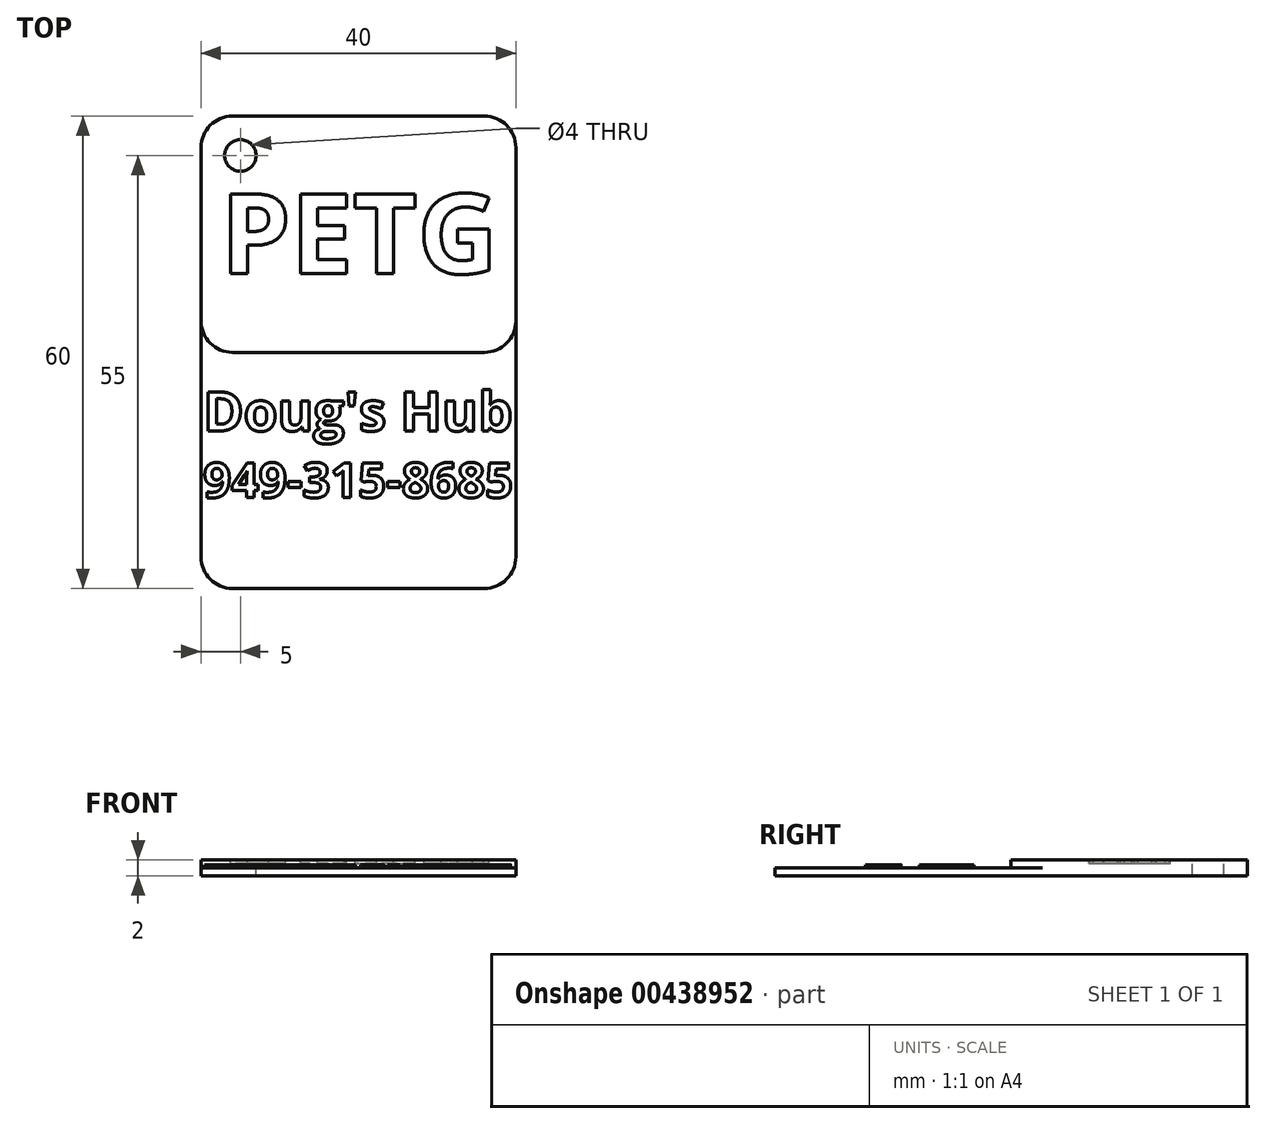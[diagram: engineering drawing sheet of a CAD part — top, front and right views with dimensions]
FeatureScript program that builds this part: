
annotation { "Feature Type Name" : "Feature", "Feature Type Description" : "" }
export const myFeature = defineFeature(function(context is Context, id is Id, definition is map)
    precondition{}
    {
        {
            var Q0;
            Q0=qCreatedBy(makeId("Top.planeOp"),FACE);
            var sketch = newSketch(context, id + "F0", { "sketchPlane" : qUnion([Q0])});
            skLineSegment(sketch, "E0.bottom", {"start": v(0, 0) * mm, "end": v(40, 0) * mm});
            skLineSegment(sketch, "E0.top", {"start": v(0, 60) * mm, "end": v(40, 60) * mm});
            skLineSegment(sketch, "E0.left", {"start": v(0, 0) * mm, "end": v(0, 60) * mm});
            skLineSegment(sketch, "E0.right", {"start": v(40, 0) * mm, "end": v(40, 60) * mm});
            skSolve(sketch);
        }
        {
            var Q0;
            Q0=qSketchRegion(id+"F0",true);
            extrude(context, id + "F1", {"entities" : qUnion([Q0]), "depth" : 1 * mm});
        }
        {
            var Q0;
            Q0=makeQuery(id+"F1.opExtrude","CAP_FACE",FACE,{"disambiguationData":[OSD([sQuery(id+"F0.wireOp",EDGE,"E0.bottom"),sQuery(id+"F0.wireOp",EDGE,"E0.top"),sQuery(id+"F0.wireOp",EDGE,"E0.left"),sQuery(id+"F0.wireOp",EDGE,"E0.right")])],"isStart":false});
            var sketch = newSketch(context, id + "F2", { "sketchPlane" : qUnion([Q0])});
            skLineSegment(sketch, "E1.bottom", {"start": v(0, 60) * mm, "end": v(40, 60) * mm});
            skLineSegment(sketch, "E1.top", {"start": v(0, 30) * mm, "end": v(40, 30) * mm});
            skLineSegment(sketch, "E1.left", {"start": v(0, 60) * mm, "end": v(0, 30) * mm});
            skLineSegment(sketch, "E1.right", {"start": v(40, 60) * mm, "end": v(40, 30) * mm});
            skSolve(sketch);
        }
        {
            var Q0;
            Q0=qSketchRegion(id+"F2",true);
            extrude(context, id + "F3", {"entities" : qUnion([Q0]), "operationType" : NewBodyOperationType.ADD, "depth" : 1 * mm});
        }
        {
            var Q0;
            Q0=makeQuery(id+"F1.opExtrude","CAP_FACE",FACE,{"disambiguationData":[OSD([sQuery(id+"F0.wireOp",EDGE,"E0.bottom"),sQuery(id+"F0.wireOp",EDGE,"E0.top"),sQuery(id+"F0.wireOp",EDGE,"E0.left"),sQuery(id+"F0.wireOp",EDGE,"E0.right")])],"isStart":false});
            var sketch = newSketch(context, id + "F4", { "sketchPlane" : qUnion([Q0])});
            skPoint(sketch, "E2.oppositeSnap0", {"position": v(20, 25) * mm});
            skLineSegment(sketch, "E2.bottom", {"start": v(24.97, 0) * mm, "end": v(24.97, 0) * mm});
            skText(sketch, "E3", { "text": "Doug\'s Hub", "fontName": "OpenSans-Bold.ttf"});
            skText(sketch, "E4", { "text": "949-315-8685", "fontName": "OpenSans-Bold.ttf"});
            const initialGuessF4  = {"E3": [0.00028, 0.02, 1, 0, 0.005], "E4": [0.00028, 0.01154, 1, 0, 0.00446]};
            skSetInitialGuess(sketch, initialGuessF4);
            skSolve(sketch);
        }
        {
            var Q0;
            Q0=qSketchRegion(id+"F4",true);
            extrude(context, id + "F5", {"entities" : qUnion([Q0]), "operationType" : NewBodyOperationType.ADD, "depth" : .4 * mm});
        }
        {
            var Q0;
            Q0=makeQuery(id+"F3.opExtrude","CAP_FACE",FACE,{"disambiguationData":[OSD([sQuery(id+"F2.wireOp",EDGE,"E1.bottom"),sQuery(id+"F2.wireOp",EDGE,"E1.top"),sQuery(id+"F2.wireOp",EDGE,"E1.left"),sQuery(id+"F2.wireOp",EDGE,"E1.right")])],"isStart":false});
            var sketch = newSketch(context, id + "F6", { "sketchPlane" : qUnion([Q0])});
            skText(sketch, "E5", { "text": "PETG", "fontName": "OpenSans-Bold.ttf"});
            const initialGuessF6  = {"E5": [0.0025, 0.04, 1, 0, 0.01018]};
            skSetInitialGuess(sketch, initialGuessF6);
            skSolve(sketch);
        }
        {
            var Q0;
            Q0=qSketchRegion(id+"F6",true);
            extrude(context, id + "F7", {"entities" : qUnion([Q0]), "operationType" : NewBodyOperationType.REMOVE, "oppositeDirection" : true, "depth" : .4 * mm});
        }
        {
            var Q0;
            {var subQ0=sQuery(id+"F2.wireOp",EDGE,"E1.left");var subQ1=sQuery(id+"F2.wireOp",EDGE,"E1.top");var subQ2=sQuery(id+"F2.wireOp",EDGE,"E1.bottom");var subQ3=sQuery(id+"F2.wireOp",EDGE,"E1.right");Q0=makeQuery(id+"F7.boolean.opBoolean","SPLIT",FACE,{"disambiguationData":[TD([makeQuery(id+"F1.opExtrude","SWEPT_FACE",FACE,{"disambiguationData":[OSD([sQuery(id+"F0.wireOp",EDGE,"E0.top")])]})])],"derivedFrom":makeQuery(id+"F3.opExtrude","CAP_FACE",FACE,{"disambiguationData":[OSD([subQ2,subQ1,subQ0,subQ3])],"isStart":false})});}
            var sketch = newSketch(context, id + "F8", { "sketchPlane" : qUnion([Q0])});
            skCircle(sketch, "E6", {"center": v(5, 55) * mm, "radius": 2 * mm});
            skSolve(sketch);
        }
        {
            var Q0;
            Q0=qSketchRegion(id+"F8",true);
            extrude(context, id + "F9", {"entities" : qUnion([Q0]), "operationType" : NewBodyOperationType.REMOVE, "endBound" : BoundingType.THROUGH_ALL, "oppositeDirection" : true, "depth" : 25.4 * mm});
        }
        {
            var Q0;
            Q0=makeQuery(id+"F3.opExtrude","SWEPT_EDGE",EDGE,{"disambiguationData":[OSD([sQuery(id+"F0.wireOp",EDGE,"E0.left"),sQuery(id+"F2.wireOp",EDGE,"E1.top"),sQuery(id+"F2.wireOp",EDGE,"E1.left")])]});
            var Q1;
            Q1=makeQuery(id+"F3.opExtrude","SWEPT_EDGE",EDGE,{"disambiguationData":[OSD([sQuery(id+"F0.wireOp",EDGE,"E0.right"),sQuery(id+"F2.wireOp",EDGE,"E1.top"),sQuery(id+"F2.wireOp",EDGE,"E1.right")])]});
            var Q2;
            Q2=makeQuery(id+"F1.opExtrude","SWEPT_EDGE",EDGE,{"disambiguationData":[OSD([sQuery(id+"F0.wireOp",EDGE,"E0.bottom"),sQuery(id+"F0.wireOp",EDGE,"E0.left")])]});
            var Q3;
            Q3=makeQuery(id+"F1.opExtrude","SWEPT_EDGE",EDGE,{"disambiguationData":[OSD([sQuery(id+"F0.wireOp",EDGE,"E0.bottom"),sQuery(id+"F0.wireOp",EDGE,"E0.right")])]});
            var Q4;
            Q4=makeQuery(id+"F3.boolean.opBoolean","MERGE",EDGE,{"derivedFrom":[makeQuery(id+"F1.opExtrude","SWEPT_EDGE",EDGE,{"disambiguationData":[OSD([sQuery(id+"F0.wireOp",EDGE,"E0.top"),sQuery(id+"F0.wireOp",EDGE,"E0.right")])]}),makeQuery(id+"F3.opExtrude","SWEPT_EDGE",EDGE,{"disambiguationData":[OSD([sQuery(id+"F2.wireOp",EDGE,"E1.bottom"),sQuery(id+"F2.wireOp",EDGE,"E1.right")])]})]});
            var Q5;
            Q5=makeQuery(id+"F3.boolean.opBoolean","MERGE",EDGE,{"derivedFrom":[makeQuery(id+"F1.opExtrude","SWEPT_EDGE",EDGE,{"disambiguationData":[OSD([sQuery(id+"F0.wireOp",EDGE,"E0.top"),sQuery(id+"F0.wireOp",EDGE,"E0.left")])]}),makeQuery(id+"F3.opExtrude","SWEPT_EDGE",EDGE,{"disambiguationData":[OSD([sQuery(id+"F2.wireOp",EDGE,"E1.bottom"),sQuery(id+"F2.wireOp",EDGE,"E1.left")])]})]});
            fillet(context, id + "F10", {"entities" : qUnion([Q0, Q1, Q2, Q3, Q4, Q5]), "radius" : 4 * mm, "tangentPropagation" : true, "allowEdgeOverflow" : false});
        }
    });
